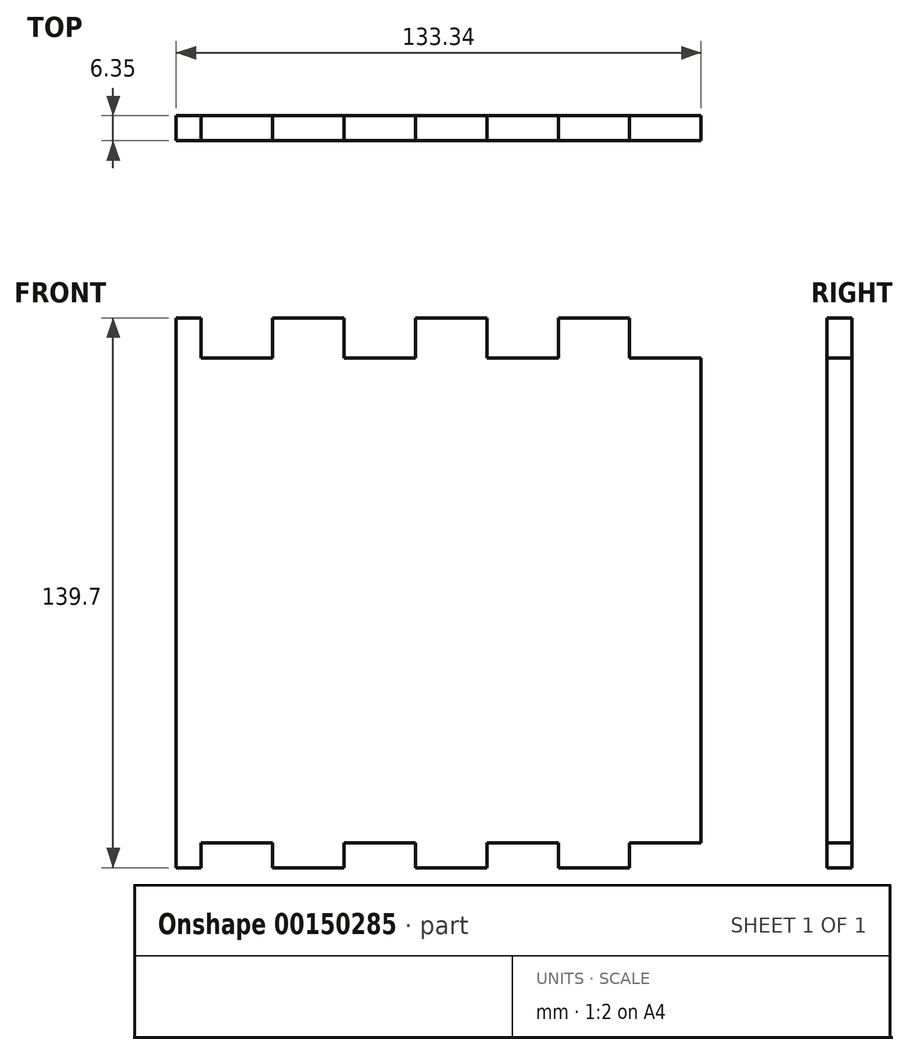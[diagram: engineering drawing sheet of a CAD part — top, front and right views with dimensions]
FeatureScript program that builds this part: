
annotation { "Feature Type Name" : "Feature", "Feature Type Description" : "" }
export const myFeature = defineFeature(function(context is Context, id is Id, definition is map)
    precondition{}
    {
        {
            var Q0;
            Q0=qCreatedBy(makeId("Front.planeOp"),FACE);
            var sketch = newSketch(context, id + "F0", { "sketchPlane" : qUnion([Q0])});
            skLineSegment(sketch, "E0.bottom", {"start": v(-66.68, 69.85) * mm, "end": v(66.67, 69.85) * mm});
            skLineSegment(sketch, "E0.top", {"start": v(-66.68, -69.85) * mm, "end": v(66.67, -69.85) * mm});
            skLineSegment(sketch, "E0.left", {"start": v(-66.68, 69.85) * mm, "end": v(-66.68, -69.85) * mm});
            skLineSegment(sketch, "E0.right", {"start": v(66.67, 69.85) * mm, "end": v(66.67, -69.85) * mm});
            skSolve(sketch);
        }
        {
            var Q0;
            Q0 = qSketchRegion(id + "F0", true);
            extrude(context, id + "F1", {"entities" : qUnion([Q0]), "depth" : 6.35 * mm});
        }
        {
            var Q0;
            Q0=makeQuery(id+"F1.opExtrude","CAP_FACE",FACE,{"disambiguationData":[OSD([sQuery(id+"F0.wireOp",EDGE,"E0.bottom"),sQuery(id+"F0.wireOp",EDGE,"E0.top"),sQuery(id+"F0.wireOp",EDGE,"E0.left"),sQuery(id+"F0.wireOp",EDGE,"E0.right")])],"isStart":false});
            var sketch = newSketch(context, id + "F2", { "sketchPlane" : qUnion([Q0])});
            skLineSegment(sketch, "E1.bottom", {"start": v(-66.68, 69.85) * mm, "end": v(66.67, 69.85) * mm});
            skLineSegment(sketch, "E1.top", {"start": v(-66.68, 59.69) * mm, "end": v(66.67, 59.69) * mm});
            skLineSegment(sketch, "E1.left", {"start": v(-66.68, 69.85) * mm, "end": v(-66.68, 59.69) * mm});
            skLineSegment(sketch, "E1.right", {"start": v(66.67, 69.85) * mm, "end": v(66.67, 59.69) * mm});
            skLineSegment(sketch, "E2", {"start": v(-60.33, 69.85) * mm, "end": v(-60.33, 59.7) * mm});
            skLineSegment(sketch, "E3", {"start": v(-42.18, 69.85) * mm, "end": v(-42.18, 59.7) * mm});
            skLineSegment(sketch, "E4", {"start": v(-24.04, 69.85) * mm, "end": v(-24.04, 59.7) * mm});
            skLineSegment(sketch, "E5", {"start": v(-5.9, 69.85) * mm, "end": v(-5.9, 59.7) * mm});
            skLineSegment(sketch, "E6", {"start": v(12.25, 69.85) * mm, "end": v(12.25, 59.7) * mm});
            skLineSegment(sketch, "E7", {"start": v(30.39, 69.85) * mm, "end": v(30.39, 59.7) * mm});
            skLineSegment(sketch, "E8", {"start": v(48.53, 69.85) * mm, "end": v(48.53, 59.7) * mm});
            skLineSegment(sketch, "E9.bottom", {"start": v(-66.68, -63.5) * mm, "end": v(66.67, -63.5) * mm});
            skLineSegment(sketch, "E9.top", {"start": v(-66.68, -69.85) * mm, "end": v(66.67, -69.85) * mm});
            skLineSegment(sketch, "E9.left", {"start": v(-66.68, -63.5) * mm, "end": v(-66.68, -69.85) * mm});
            skLineSegment(sketch, "E9.right", {"start": v(66.67, -63.5) * mm, "end": v(66.67, -69.85) * mm});
            skLineSegment(sketch, "E10", {"start": v(-60.33, 59.7) * mm, "end": v(-60.32, -69.85) * mm});
            skLineSegment(sketch, "E11", {"start": v(-42.18, 59.7) * mm, "end": v(-42.18, -69.85) * mm});
            skLineSegment(sketch, "E12", {"start": v(-24.04, 59.69) * mm, "end": v(-24.04, -69.85) * mm});
            skLineSegment(sketch, "E13", {"start": v(-5.9, 59.69) * mm, "end": v(-5.9, -69.85) * mm});
            skPoint(sketch, "E13.endSnap0", {"position": v(0, -69.85) * mm});
            skLineSegment(sketch, "E14", {"start": v(12.25, 59.7) * mm, "end": v(12.25, -69.85) * mm});
            skLineSegment(sketch, "E15", {"start": v(30.39, 59.69) * mm, "end": v(30.39, -69.85) * mm});
            skLineSegment(sketch, "E16", {"start": v(48.53, 59.7) * mm, "end": v(48.53, -69.85) * mm});
            skSolve(sketch);
        }
        {
            var Q0;
            {var subQ0=sQuery(id+"F2.wireOp",EDGE,"E1.right");Q0=makeQuery(id+"F2.imprint","IMPRINT",FACE,{"disambiguationData":[TD([[makeQuery(id+"F2.imprint","IMPRINT",EDGE,{"derivedFrom":subQ0}),-1.0]])]});}
            var Q1;
            {var subQ0=sQuery(id+"F2.wireOp",EDGE,"E2");Q1=makeQuery(id+"F2.imprint","IMPRINT",FACE,{"disambiguationData":[TD([[makeQuery(id+"F2.imprint","IMPRINT",EDGE,{"derivedFrom":subQ0}),1.0]])]});}
            var Q2;
            {var subQ0=sQuery(id+"F2.wireOp",EDGE,"E4");Q2=makeQuery(id+"F2.imprint","IMPRINT",FACE,{"disambiguationData":[TD([[makeQuery(id+"F2.imprint","IMPRINT",EDGE,{"derivedFrom":subQ0}),1.0]])]});}
            var Q3;
            {var subQ0=sQuery(id+"F2.wireOp",EDGE,"E6");Q3=makeQuery(id+"F2.imprint","IMPRINT",FACE,{"disambiguationData":[TD([[makeQuery(id+"F2.imprint","IMPRINT",EDGE,{"derivedFrom":subQ0}),1.0]])]});}
            var Q4;
            {var subQ0=sQuery(id+"F2.wireOp",EDGE,"E10");var subQ1=sQuery(id+"F2.wireOp",EDGE,"E9.bottom");var subQ2=makeQuery(id+"F2.imprint","INTERSECT",VERTEX,{"derivedFrom":[subQ1,subQ0]});Q4=makeQuery(id+"F2.imprint","IMPRINT",FACE,{"disambiguationData":[TD([[makeQuery(id+"F2.imprint","IMPRINT",EDGE,{"disambiguationData":[TD([[subQ2,-1.0]])],"derivedFrom":subQ1}),-1.0]])]});}
            var Q5;
            {var subQ0=sQuery(id+"F2.wireOp",EDGE,"E12");var subQ1=sQuery(id+"F2.wireOp",EDGE,"E9.bottom");var subQ2=makeQuery(id+"F2.imprint","INTERSECT",VERTEX,{"derivedFrom":[subQ1,subQ0]});Q5=makeQuery(id+"F2.imprint","IMPRINT",FACE,{"disambiguationData":[TD([[makeQuery(id+"F2.imprint","IMPRINT",EDGE,{"disambiguationData":[TD([[subQ2,-1.0]])],"derivedFrom":subQ1}),-1.0]])]});}
            var Q6;
            {var subQ0=sQuery(id+"F2.wireOp",EDGE,"E14");var subQ1=sQuery(id+"F2.wireOp",EDGE,"E9.bottom");var subQ2=makeQuery(id+"F2.imprint","INTERSECT",VERTEX,{"derivedFrom":[subQ1,subQ0]});Q6=makeQuery(id+"F2.imprint","IMPRINT",FACE,{"disambiguationData":[TD([[makeQuery(id+"F2.imprint","IMPRINT",EDGE,{"disambiguationData":[TD([[subQ2,-1.0]])],"derivedFrom":subQ1}),-1.0]])]});}
            var Q7;
            {var subQ0=sQuery(id+"F2.wireOp",EDGE,"E9.right");Q7=makeQuery(id+"F2.imprint","IMPRINT",FACE,{"disambiguationData":[TD([[makeQuery(id+"F2.imprint","IMPRINT",EDGE,{"derivedFrom":subQ0}),-1.0]])]});}
            extrude(context, id + "F3", {"entities" : qUnion([Q0, Q1, Q2, Q3, Q4, Q5, Q6, Q7]), "operationType" : NewBodyOperationType.REMOVE, "oppositeDirection" : true, "depth" : 25.4 * mm});
        }
    });
